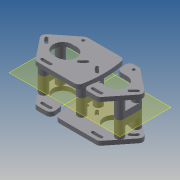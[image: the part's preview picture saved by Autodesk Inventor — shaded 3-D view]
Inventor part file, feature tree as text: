
AUTODESK INVENTOR PART (.ipt)
format: ipt  version: 2013 (Build 170138000, 138)  size: 384,512 bytes
history: native  units: mm
features: extrude x4, sketch x4, mirror x2, fillet x2, pattern_linear x1, plane x1, other x1, pattern_circular x1, projected_geometry x1
ambient origin geometry x8: Origin, YZ Plane, XZ Plane, XY Plane, X Axis, Y Axis, Z Axis, Center Point
bodies: Solid1 (feature_tree)
feature tree (17):
  extrude  "Extrusion1"  Depth=31.0mm
  mirror  "Mirror1"
  pattern_linear  "Rectangular Pattern1"  Spacing1=5.0mm  [1 undecoded]
  extrude  "Extrusion2"  Depth=3.5mm
  mirror  "Mirror2"
  plane  "Work Plane1"
  extrude  "Extrusion3"  Depth=11.25mm
  extrude  "Extrusion4"  Depth=1.142982mm
  fillet  "Fillet2"  Radius=20.0mm
  other  "Work Axis1"
  pattern_circular  "Circular Pattern1"  [2 undecoded]
  fillet  "Fillet3"  Radius=1.142982mm
  sketch  "Sketch1"  dims[d0=30.0mm d1=31.0mm]
  sketch  "Sketch3"  dims[d2=42.0mm]
  sketch  "Sketch4"  dims[d3=5.0mm]
  sketch  "Sketch5"  dims[d4=3.5mm d5=5.0mm d6=3.5mm d7=11.25mm d8=1.142982mm d10=20.0mm d12=90.0deg d15=5.0mm d16=0.0mm d18=1.142982mm d19=5.5mm d20=5.5mm d21=5.5mm d22=5.5mm d23=5.5mm d24=5.5mm d25=20.0mm d27=45.0mm d28=150.0mm d30=159.0mm d31=10.0mm d32=9.75mm d33=5.0mm d34=0.0mm d35=15.0mm d36=0.0mm d37=5.0mm d40=30.0mm d41=0.0mm d42=5.5mm d43=20.0mm d44=360.0deg d46=5.5mm]
  projected_geometry  "Project Cut Edges1"
note: 3 required parameter values undecoded (feature->parameter linkage not recoverable at this tier; creation-order binding heuristic only, values carry confidence <= 0.55)
